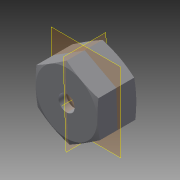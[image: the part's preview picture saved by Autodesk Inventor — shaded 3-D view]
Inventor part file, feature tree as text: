
AUTODESK INVENTOR PART (.ipt)
format: ipt  version: 2018 (Build 220112000, 112)  size: 128,512 bytes
history: native  units: in
note: dims shown in document units (in); Inventor stores cm internally (conversion verified against a paired STEP export)
features: sketch x4, plane x3, extrude x3, reference x2, thread x1, other x1, revolve x1, mirror x1
ambient origin geometry x8: Origin, YZ Plane, XZ Plane, XY Plane, X Axis, Y Axis, Z Axis, Center Point
bodies: Body1 (feature_tree)
feature tree (16):
  plane  "Work Plane3"
  extrude  "Extrusion2"  Depth=0.5in
  extrude  "Extrusion3"  Depth=0.375in TaperAngle=0.0deg
  extrude  "Extrusion4"  TaperAngle=90.0deg  [1 undecoded]
  thread  "Thread1"  [1 undecoded]
  plane  "Work Plane4"
  other  "Work Axis4"
  revolve  "Revolution2"  [1 undecoded]
  plane  "Work Plane5"
  mirror  "Mirror1"
  sketch  "Sketch6"  dims[d3=0.3125in d4=0.0in d5=0.5in]
  sketch  "Sketch7"  dims[d6=0.25in d7=-0.0123in d8=0.375in d9=0.0in]
  reference  "Reference1"
  sketch  "Sketch8"  dims[d10=0.392in d11=0.0in d12=90.0deg d13=0.045in]
  reference  "Reference2"
  sketch  "Sketch9"
note: 3 required parameter values undecoded (feature->parameter linkage not recoverable at this tier; creation-order binding heuristic only, values carry confidence <= 0.55)
